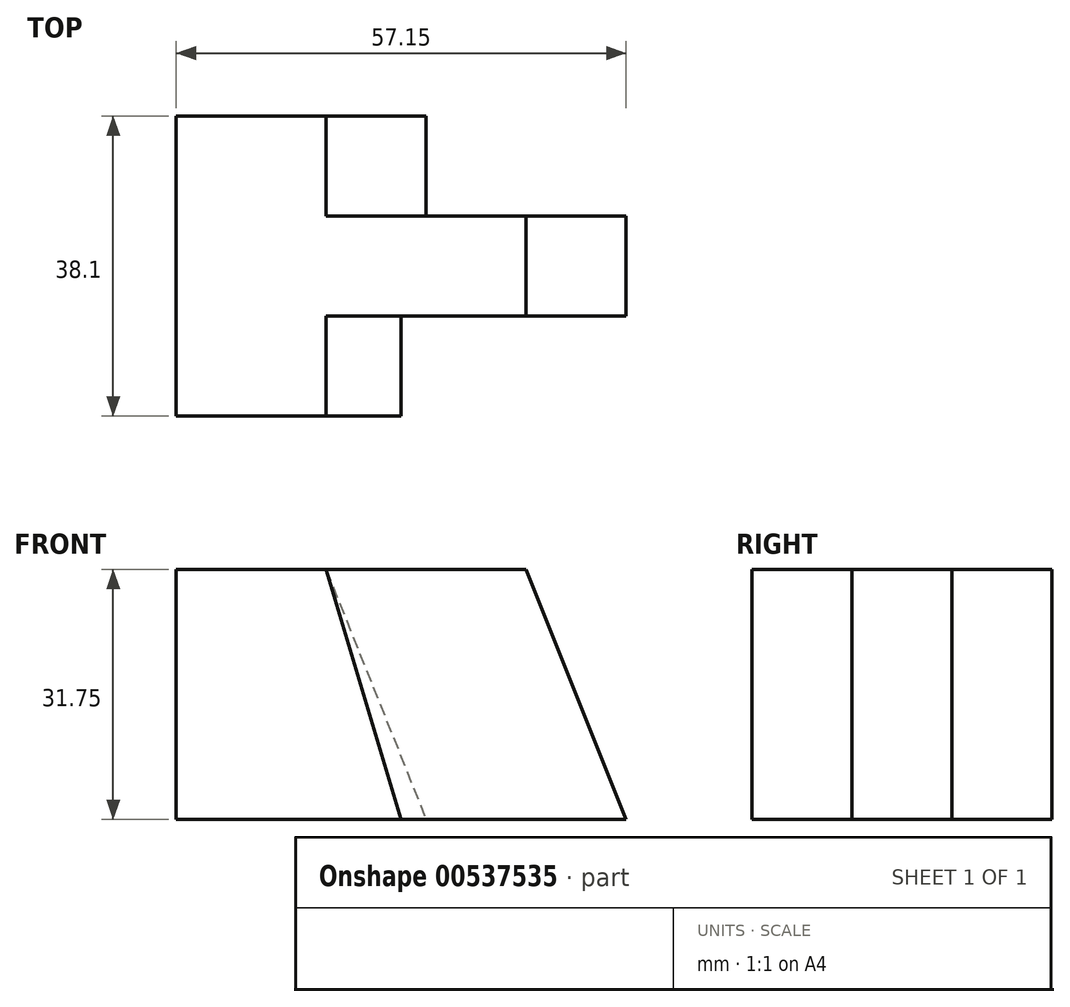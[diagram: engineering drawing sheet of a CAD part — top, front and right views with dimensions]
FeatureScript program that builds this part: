
annotation { "Feature Type Name" : "Feature", "Feature Type Description" : "" }
export const myFeature = defineFeature(function(context is Context, id is Id, definition is map)
    precondition{}
    {
        {
            var Q0;
            Q0=qCreatedBy(makeId("Front.planeOp"),FACE);
            var sketch = newSketch(context, id + "F0", { "sketchPlane" : qUnion([Q0])});
            skLineSegment(sketch, "E0", {"start": v(0, 0) * mm, "end": v(0, 31.75) * mm});
            skLineSegment(sketch, "E1", {"start": v(0, 31.75) * mm, "end": v(57.15, 31.75) * mm});
            skLineSegment(sketch, "E2", {"start": v(57.15, 31.75) * mm, "end": v(57.15, 0) * mm});
            skLineSegment(sketch, "E3", {"start": v(57.15, 0) * mm, "end": v(0, 0) * mm});
            skSolve(sketch);
        }
        {
            var Q0;
            Q0 = qSketchRegion(id + "F0", true);
            extrude(context, id + "F1", {"entities" : qUnion([Q0]), "depth" : 38.1 * mm, "offsetDistance" : 25.4 * mm});
        }
        {
            var Q0;
            Q0=makeQuery(id+"F1.opExtrude","CAP_FACE",FACE,{"disambiguationData":[OSD([sQuery(id+"F0.wireOp",EDGE,"E0"),sQuery(id+"F0.wireOp",EDGE,"E1"),sQuery(id+"F0.wireOp",EDGE,"E2"),sQuery(id+"F0.wireOp",EDGE,"E3")])],"isStart":false});
            var sketch = newSketch(context, id + "F2", { "sketchPlane" : qUnion([Q0])});
            skLineSegment(sketch, "E4", {"start": v(19.05, 31.75) * mm, "end": v(28.58, 0) * mm});
            skSolve(sketch);
        }
        {
            var Q0;
            {var subQ0=sQuery(id+"F2.wireOp",EDGE,"E4");Q0=makeQuery(id+"F2.imprint","IMPRINT",FACE,{"disambiguationData":[TD([[makeQuery(id+"F2.imprint","IMPRINT",EDGE,{"derivedFrom":subQ0}),1.0]])]});}
            extrude(context, id + "F3", {"entities" : qUnion([Q0]), "operationType" : NewBodyOperationType.REMOVE, "oppositeDirection" : true, "depth" : 12.7 * mm, "offsetDistance" : 25.4 * mm});
        }
        {
            var Q0;
            Q0=makeQuery(id+"F1.opExtrude","CAP_FACE",FACE,{"disambiguationData":[OSD([sQuery(id+"F0.wireOp",EDGE,"E0"),sQuery(id+"F0.wireOp",EDGE,"E1"),sQuery(id+"F0.wireOp",EDGE,"E2"),sQuery(id+"F0.wireOp",EDGE,"E3")])],"isStart":true});
            var sketch = newSketch(context, id + "F4", { "sketchPlane" : qUnion([Q0])});
            skLineSegment(sketch, "E5", {"start": v(-19.05, 31.75) * mm, "end": v(-31.75, 0) * mm});
            skSolve(sketch);
        }
        {
            var Q0;
            {var subQ0=sQuery(id+"F4.wireOp",EDGE,"E5");Q0=makeQuery(id+"F4.imprint","IMPRINT",FACE,{"disambiguationData":[TD([[makeQuery(id+"F4.imprint","IMPRINT",EDGE,{"derivedFrom":subQ0}),-1.0]])]});}
            extrude(context, id + "F5", {"entities" : qUnion([Q0]), "operationType" : NewBodyOperationType.REMOVE, "oppositeDirection" : true, "depth" : 12.7 * mm, "offsetDistance" : 25.4 * mm});
        }
        {
            var Q0;
            Q0=makeQuery(id+"F3.boolean.opBoolean","COPY",FACE,{"derivedFrom":makeQuery(id+"F3.opExtrude","CAP_FACE",FACE,{"disambiguationData":[OSD([sQuery(id+"F0.wireOp",EDGE,"E1"),sQuery(id+"F0.wireOp",EDGE,"E2"),sQuery(id+"F0.wireOp",EDGE,"E3"),sQuery(id+"F2.wireOp",EDGE,"E4")])],"isStart":false})});
            var sketch = newSketch(context, id + "F6", { "sketchPlane" : qUnion([Q0])});
            skLineSegment(sketch, "E6", {"start": v(44.45, 31.75) * mm, "end": v(57.15, 0) * mm});
            skSolve(sketch);
        }
        {
            var Q0;
            {var subQ0=sQuery(id+"F6.wireOp",EDGE,"E6");Q0=makeQuery(id+"F6.imprint","IMPRINT",FACE,{"disambiguationData":[TD([[makeQuery(id+"F6.imprint","IMPRINT",EDGE,{"derivedFrom":subQ0}),1.0]])]});}
            extrude(context, id + "F7", {"entities" : qUnion([Q0]), "operationType" : NewBodyOperationType.REMOVE, "oppositeDirection" : true, "depth" : 25.4 * mm, "offsetDistance" : 25.4 * mm});
        }
    });
